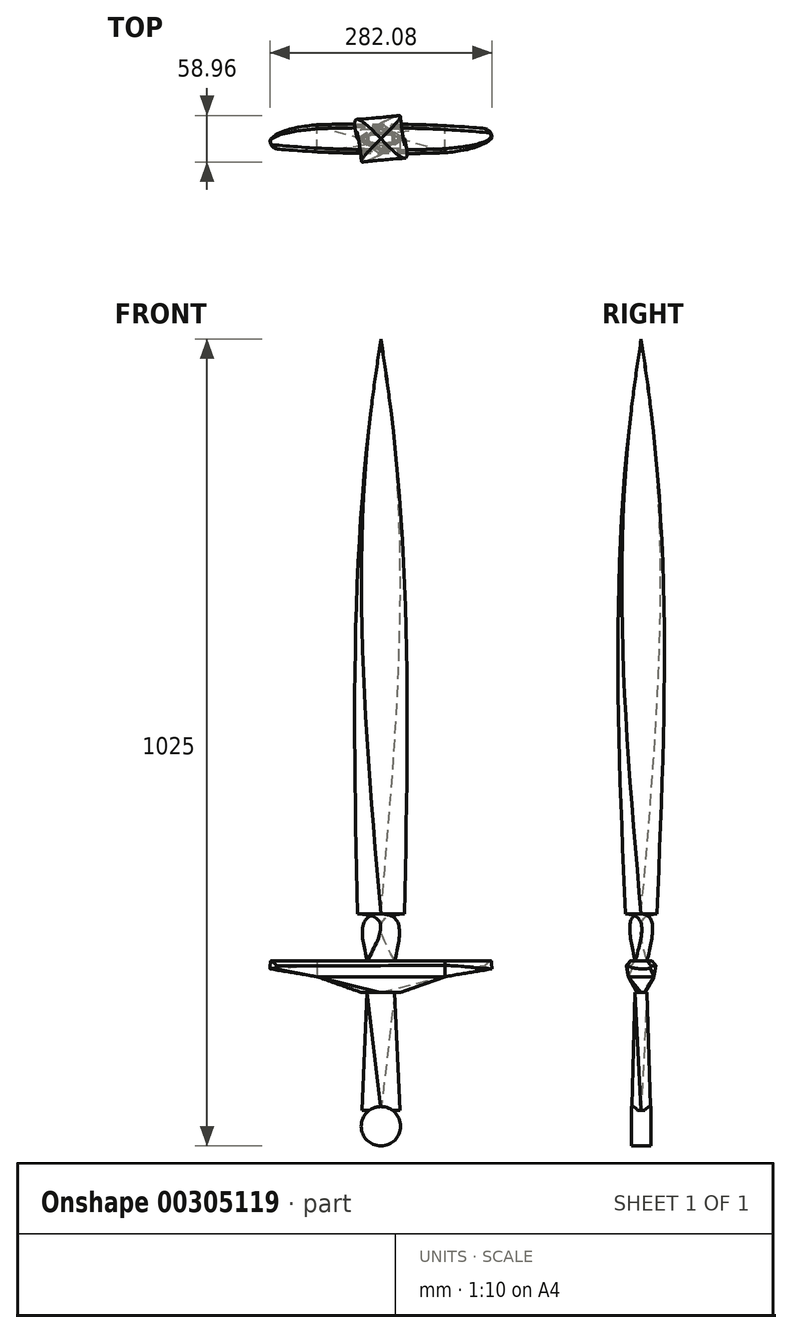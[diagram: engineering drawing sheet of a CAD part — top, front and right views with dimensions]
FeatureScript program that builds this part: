
annotation { "Feature Type Name" : "Feature", "Feature Type Description" : "" }
export const myFeature = defineFeature(function(context is Context, id is Id, definition is map)
    precondition{}
    {
        {
            var Q0;
            Q0=qCreatedBy(makeId("Top.planeOp"),FACE);
            cPlane(context, id + "F0", {"entities" : qUnion([Q0]), "cplaneType" : CPlaneType.OFFSET, "offset" : 57.5 * mm, "width" : 150 * mm, "height" : 150 * mm});
        }
        {
            var Q0;
            Q0=qCreatedBy(id+"F0.planeOp",FACE);
            cPlane(context, id + "F1", {"entities" : qUnion([Q0]), "cplaneType" : CPlaneType.OFFSET, "offset" : 2.5 * mm, "width" : 150 * mm, "height" : 150 * mm});
        }
        {
            var Q0;
            Q0=qCreatedBy(makeId("Top.planeOp"),FACE);
            cPlane(context, id + "F2", {"entities" : qUnion([Q0]), "cplaneType" : CPlaneType.OFFSET, "offset" : 20 * mm, "oppositeDirection" : true, "width" : 150 * mm, "height" : 150 * mm});
        }
        {
            var Q0;
            Q0=qCreatedBy(id+"F2.planeOp",FACE);
            cPlane(context, id + "F3", {"entities" : qUnion([Q0]), "cplaneType" : CPlaneType.OFFSET, "offset" : 20 * mm, "oppositeDirection" : true, "width" : 150 * mm, "height" : 150 * mm});
        }
        {
            var Q0;
            Q0=qCreatedBy(id+"F1.planeOp",FACE);
            cPlane(context, id + "F4", {"entities" : qUnion([Q0]), "cplaneType" : CPlaneType.OFFSET, "offset" : 640 * mm, "width" : 150 * mm, "height" : 150 * mm});
        }
        {
            var Q0;
            Q0=qCreatedBy(id+"F4.planeOp",FACE);
            cPlane(context, id + "F5", {"entities" : qUnion([Q0]), "cplaneType" : CPlaneType.OFFSET, "offset" : 90 * mm, "width" : 150 * mm, "height" : 150 * mm});
        }
        {
            var Q0;
            Q0=qCreatedBy(id+"F3.planeOp",FACE);
            cPlane(context, id + "F6", {"entities" : qUnion([Q0]), "cplaneType" : CPlaneType.OFFSET, "offset" : 150 * mm, "oppositeDirection" : true, "width" : 150 * mm, "height" : 150 * mm});
        }
        {
            var Q0;
            Q0=qCreatedBy(id+"F4.planeOp",FACE);
            var sketch = newSketch(context, id + "F7", { "sketchPlane" : qUnion([Q0])});
            skLineSegment(sketch, "E0.bottom", {"start": v(12.5, 12.5) * mm, "end": v(-12.5, 12.5) * mm});
            skLineSegment(sketch, "E0.top", {"start": v(12.5, -12.5) * mm, "end": v(-12.5, -12.5) * mm});
            skLineSegment(sketch, "E0.left", {"start": v(12.5, 12.5) * mm, "end": v(12.5, -12.5) * mm});
            skLineSegment(sketch, "E0.right", {"start": v(-12.5, 12.5) * mm, "end": v(-12.5, -12.5) * mm});
            skPoint(sketch, "E0.middle", {"position": v(0, 0) * mm});
            skSolve(sketch);
        }
        {
            var Q0;
            Q0=qCreatedBy(makeId("Top.planeOp"),FACE);
            var sketch = newSketch(context, id + "F8", { "sketchPlane" : qUnion([Q0])});
            skLineSegment(sketch, "E1.bottom", {"start": v(17.5, -7.5) * mm, "end": v(-17.5, -7.5) * mm});
            skLineSegment(sketch, "E1.top", {"start": v(17.5, 7.5) * mm, "end": v(-17.5, 7.5) * mm});
            skLineSegment(sketch, "E1.left", {"start": v(17.5, -7.5) * mm, "end": v(17.5, 7.5) * mm});
            skLineSegment(sketch, "E1.right", {"start": v(-17.5, -7.5) * mm, "end": v(-17.5, 7.5) * mm});
            skPoint(sketch, "E1.middle", {"position": v(0, 0) * mm});
            skSolve(sketch);
        }
        {
            var Q0;
            Q0=qCreatedBy(id+"F0.planeOp",FACE);
            var sketch = newSketch(context, id + "F9", { "sketchPlane" : qUnion([Q0])});
            skLineSegment(sketch, "E2", {"start": v(0, 0) * mm, "end": v(0, 16.67) * mm, "construction": true});
            skLineSegment(sketch, "E3", {"start": v(0, 16.67) * mm, "end": v(-25, 0) * mm});
            skLineSegment(sketch, "E4", {"start": v(-25, 0) * mm, "end": v(0, -16.67) * mm});
            skLineSegment(sketch, "E5", {"start": v(0, -16.67) * mm, "end": v(25, 0) * mm});
            skLineSegment(sketch, "E6", {"start": v(25, 0) * mm, "end": v(0, 16.67) * mm});
            skLineSegment(sketch, "E7", {"start": v(0, 0) * mm, "end": v(25, 0) * mm, "construction": true});
            skLineSegment(sketch, "E8.bottom", {"start": v(-12.5, -8.33) * mm, "end": v(12.5, -8.33) * mm});
            skLineSegment(sketch, "E8.top", {"start": v(-12.5, 8.33) * mm, "end": v(12.5, 8.33) * mm});
            skLineSegment(sketch, "E8.left", {"start": v(-12.5, -8.33) * mm, "end": v(-12.5, 8.33) * mm});
            skLineSegment(sketch, "E8.right", {"start": v(12.5, -8.33) * mm, "end": v(12.5, 8.33) * mm});
            skSolve(sketch);
        }
        {
            var Q0;
            Q0=qCreatedBy(id+"F1.planeOp",FACE);
            var sketch = newSketch(context, id + "F10", { "sketchPlane" : qUnion([Q0])});
            skLineSegment(sketch, "E9", {"start": v(0, 0) * mm, "end": v(0, 20) * mm, "construction": true});
            skLineSegment(sketch, "E10", {"start": v(0, 20) * mm, "end": v(30, 0) * mm});
            skLineSegment(sketch, "E11", {"start": v(30, 0) * mm, "end": v(0, -20) * mm});
            skLineSegment(sketch, "E12", {"start": v(0, -20) * mm, "end": v(-30, 0) * mm});
            skLineSegment(sketch, "E13", {"start": v(-30, 0) * mm, "end": v(0, 20) * mm});
            skLineSegment(sketch, "E14", {"start": v(0, 0) * mm, "end": v(-30, 0) * mm, "construction": true});
            skSolve(sketch);
        }
        {
            var Q0;
            Q0=qCreatedBy(makeId("Top.planeOp"),FACE);
            var sketch = newSketch(context, id + "F11", { "sketchPlane" : qUnion([Q0])});
            skPoint(sketch, "E15.middle", {"position": v(0, 0) * mm});
            skLineSegment(sketch, "E16", {"start": v(0, 0) * mm, "end": v(-200, 0) * mm, "construction": true});
            skEllipse(sketch, "E17", {"center": v(0, 0) * mm, "majorRadius": 200 * mm, "minorRadius": 20 * mm, "majorAxis": v(-1, 0)});
            skSolve(sketch);
        }
        {
            var Q0;
            Q0=qCreatedBy(id+"F2.planeOp",FACE);
            var sketch = newSketch(context, id + "F12", { "sketchPlane" : qUnion([Q0])});
            skLineSegment(sketch, "E18.bottom", {"start": v(81.25, -16.25) * mm, "end": v(-81.25, -16.25) * mm});
            skLineSegment(sketch, "E18.top", {"start": v(81.25, 16.25) * mm, "end": v(-81.25, 16.25) * mm});
            skLineSegment(sketch, "E18.left", {"start": v(81.25, -16.25) * mm, "end": v(81.25, 16.25) * mm});
            skLineSegment(sketch, "E18.right", {"start": v(-81.25, -16.25) * mm, "end": v(-81.25, 16.25) * mm});
            skPoint(sketch, "E18.middle", {"position": v(0, 0) * mm});
            skSolve(sketch);
        }
        {
            var Q0;
            Q0=qCreatedBy(id+"F3.planeOp",FACE);
            var sketch = newSketch(context, id + "F13", { "sketchPlane" : qUnion([Q0])});
            skPoint(sketch, "E19.middle", {"position": v(0, 0) * mm});
            skLineSegment(sketch, "E20", {"start": v(0, 0) * mm, "end": v(-25, 0) * mm, "construction": true});
            skEllipse(sketch, "E21", {"center": v(0, 0) * mm, "majorRadius": 25 * mm, "minorRadius": 5 * mm, "majorAxis": v(-1, 0)});
            skSolve(sketch);
        }
        {
            var Q0;
            Q0=qCreatedBy(makeId("Front.planeOp"),FACE);
            var sketch = newSketch(context, id + "F14", { "sketchPlane" : qUnion([Q0])});
            skLineSegment(sketch, "E22", {"start": v(0, 0) * mm, "end": v(0, -210) * mm, "construction": true});
            skCircle(sketch, "E23", {"center": v(0, -210) * mm, "radius": 25 * mm});
            skSolve(sketch);
        }
        {
            var Q0;
            Q0=qCreatedBy(id+"F3.planeOp",FACE);
            var sketch = newSketch(context, id + "F15", { "sketchPlane" : qUnion([Q0])});
            skLineSegment(sketch, "E24.bottom", {"start": v(17.5, -7.5) * mm, "end": v(-17.5, -7.5) * mm});
            skLineSegment(sketch, "E24.top", {"start": v(17.5, 7.5) * mm, "end": v(-17.5, 7.5) * mm});
            skLineSegment(sketch, "E24.left", {"start": v(17.5, -7.5) * mm, "end": v(17.5, 7.5) * mm});
            skLineSegment(sketch, "E24.right", {"start": v(-17.5, -7.5) * mm, "end": v(-17.5, 7.5) * mm});
            skPoint(sketch, "E24.middle", {"position": v(0, 0) * mm});
            skSolve(sketch);
        }
        {
            var Q0;
            Q0=qCreatedBy(id+"F5.planeOp",FACE);
            var sketch = newSketch(context, id + "F16", { "sketchPlane" : qUnion([Q0])});
            skPoint(sketch, "E25", {"position": v(0, 0) * mm});
            skSolve(sketch);
        }
        {
            var Q0;
            Q0=qCreatedBy(id+"F6.planeOp",FACE);
            var sketch = newSketch(context, id + "F17", { "sketchPlane" : qUnion([Q0])});
            skLineSegment(sketch, "E26", {"start": v(0, 0) * mm, "end": v(0, -12) * mm, "construction": true});
            skLineSegment(sketch, "E27", {"start": v(0, -12) * mm, "end": v(-24, 0) * mm});
            skLineSegment(sketch, "E28", {"start": v(-24, 0) * mm, "end": v(0, 12) * mm});
            skLineSegment(sketch, "E29", {"start": v(0, 12) * mm, "end": v(24, 0) * mm});
            skLineSegment(sketch, "E30", {"start": v(24, 0) * mm, "end": v(0, -12) * mm});
            skLineSegment(sketch, "E31", {"start": v(0, 0) * mm, "end": v(24, 0) * mm, "construction": true});
            skSolve(sketch);
        }
        {
            var Q0;
            Q0=makeQuery(id+"F11.imprint","IMPRINT",FACE,{"disambiguationData":[TD([[makeQuery(id+"F11.imprint","IMPRINT",EDGE,{"derivedFrom":sQuery(id+"F11.wireOp",EDGE,"E17")}),1.0]])]});
            var Q1;
            Q1=makeQuery(id+"F12.imprint","IMPRINT",FACE,{"disambiguationData":[TD([[makeQuery(id+"F12.imprint","IMPRINT",EDGE,{"derivedFrom":sQuery(id+"F12.wireOp",EDGE,"E18.bottom")}),-1.0]])]});
            loft(context, id + "F18", {"sheetProfilesArray" : [{ "sheetProfileEntities" : qUnion([Q0]) }, { "sheetProfileEntities" : qUnion([Q1]) }]});
        }
        {
            var Q1;
            Q1=makeQuery(id+"F12.imprint","IMPRINT",FACE,{"disambiguationData":[TD([[makeQuery(id+"F12.imprint","IMPRINT",EDGE,{"derivedFrom":sQuery(id+"F12.wireOp",EDGE,"E18.bottom")}),-1.0]])]});
            var Q2;
            Q2=makeQuery(id+"F13.imprint","IMPRINT",FACE,{"disambiguationData":[TD([[makeQuery(id+"F13.imprint","IMPRINT",EDGE,{"derivedFrom":sQuery(id+"F13.wireOp",EDGE,"E21")}),1.0]])]});
            loft(context, id + "F19", {"operationType" : NewBodyOperationType.ADD, "sheetProfilesArray" : [{ "sheetProfileEntities" : qUnion([Q1]) }, { "sheetProfileEntities" : qUnion([Q2]) }]});
        }
        {
            var Q1;
            Q1=makeQuery(id+"F8.imprint","IMPRINT",FACE,{"disambiguationData":[TD([[makeQuery(id+"F8.imprint","IMPRINT",EDGE,{"derivedFrom":sQuery(id+"F8.wireOp",EDGE,"E1.bottom")}),-1.0]])]});
            var Q2;
            Q2=makeQuery(id+"F9.imprint","IMPRINT",FACE,{"disambiguationData":[TD([[makeQuery(id+"F9.imprint","IMPRINT",EDGE,{"derivedFrom":sQuery(id+"F9.wireOp",EDGE,"E8.bottom")}),1.0]])]});
            var Q3;
            Q3=makeQuery(id+"F10.imprint","IMPRINT",FACE,{"disambiguationData":[TD([[makeQuery(id+"F10.imprint","IMPRINT",EDGE,{"derivedFrom":sQuery(id+"F10.wireOp",EDGE,"E10")}),-1.0]])]});
            loft(context, id + "F20", {"operationType" : NewBodyOperationType.ADD, "sheetProfilesArray" : [{ "sheetProfileEntities" : qUnion([Q1]) }, { "sheetProfileEntities" : qUnion([Q2]) }, { "sheetProfileEntities" : qUnion([Q3]) }]});
        }
        {
            var Q1;
            Q1=makeQuery(id+"F10.imprint","IMPRINT",FACE,{"disambiguationData":[TD([[makeQuery(id+"F10.imprint","IMPRINT",EDGE,{"derivedFrom":sQuery(id+"F10.wireOp",EDGE,"E10")}),-1.0]])]});
            var Q2;
            Q2=makeQuery(id+"F7.imprint","IMPRINT",FACE,{"disambiguationData":[TD([[makeQuery(id+"F7.imprint","IMPRINT",EDGE,{"derivedFrom":sQuery(id+"F7.wireOp",EDGE,"E0.bottom")}),1.0]])]});
            var Q3;
            Q3=sQuery(id+"F16.wireOp",VERTEX,"E25");
            loft(context, id + "F21", {"operationType" : NewBodyOperationType.ADD, "sheetProfilesArray" : [{ "sheetProfileEntities" : qUnion([Q1]) }, { "sheetProfileEntities" : qUnion([Q2]) }, { "sheetProfileEntities" : qUnion([Q3]) }]});
        }
        {
            var Q0;
            Q0=makeQuery(id+"F14.imprint","IMPRINT",FACE,{"disambiguationData":[TD([[makeQuery(id+"F14.imprint","IMPRINT",EDGE,{"derivedFrom":sQuery(id+"F14.wireOp",EDGE,"E23")}),1.0]])]});
            extrude(context, id + "F22", {"entities" : qUnion([Q0]), "operationType" : NewBodyOperationType.ADD, "endBound" : BoundingType.SYMMETRIC, "depth" : 25 * mm});
        }
        {
            var Q1;
            Q1=makeQuery(id+"F15.imprint","IMPRINT",FACE,{"disambiguationData":[TD([[makeQuery(id+"F15.imprint","IMPRINT",EDGE,{"derivedFrom":sQuery(id+"F15.wireOp",EDGE,"E24.bottom")}),-1.0]])]});
            var Q2;
            Q2=makeQuery(id+"F17.imprint","IMPRINT",FACE,{"disambiguationData":[TD([[makeQuery(id+"F17.imprint","IMPRINT",EDGE,{"derivedFrom":sQuery(id+"F17.wireOp",EDGE,"E27")}),-1.0]])]});
            loft(context, id + "F23", {"operationType" : NewBodyOperationType.ADD, "sheetProfilesArray" : [{ "sheetProfileEntities" : qUnion([Q1]) }, { "sheetProfileEntities" : qUnion([Q2]) }]});
        }
        {
            var Q0;
            Q0=makeQuery(id+"F18.opLoft","MID_CAP_EDGE",EDGE,{"disambiguationData":[OSD([sQuery(id+"F11.wireOp",EDGE,"E17"),sQuery(id+"F12.wireOp",EDGE,"E18.bottom"),sQuery(id+"F12.wireOp",EDGE,"E18.top"),sQuery(id+"F12.wireOp",EDGE,"E18.right")])],"capPos":0.0});
            var Q1;
            Q1=makeQuery(id+"F18.opLoft","MID_CAP_EDGE",EDGE,{"disambiguationData":[OSD([sQuery(id+"F11.wireOp",EDGE,"E17"),sQuery(id+"F12.wireOp",EDGE,"E18.bottom"),sQuery(id+"F12.wireOp",EDGE,"E18.top"),sQuery(id+"F12.wireOp",EDGE,"E18.left"),sQuery(id+"F12.wireOp",EDGE,"E18.right")])],"capPos":0.0});
            var Q2;
            Q2=makeQuery(id+"F18.opLoft","MID_CAP_EDGE",EDGE,{"disambiguationData":[OSD([sQuery(id+"F11.wireOp",EDGE,"E17"),sQuery(id+"F12.wireOp",EDGE,"E18.bottom"),sQuery(id+"F12.wireOp",EDGE,"E18.left")])],"capPos":0.0});
            var Q3;
            Q3=makeQuery(id+"F18.opLoft","MID_CAP_EDGE",EDGE,{"disambiguationData":[OSD([sQuery(id+"F11.wireOp",EDGE,"E17"),sQuery(id+"F12.wireOp",EDGE,"E18.bottom"),sQuery(id+"F12.wireOp",EDGE,"E18.left"),sQuery(id+"F12.wireOp",EDGE,"E18.right")])],"capPos":0.0});
            chamfer(context, id + "F24", {"entities" : qUnion([Q0, Q1, Q2, Q3]), "width" : 5 * mm, "tangentPropagation" : true});
        }
    });
